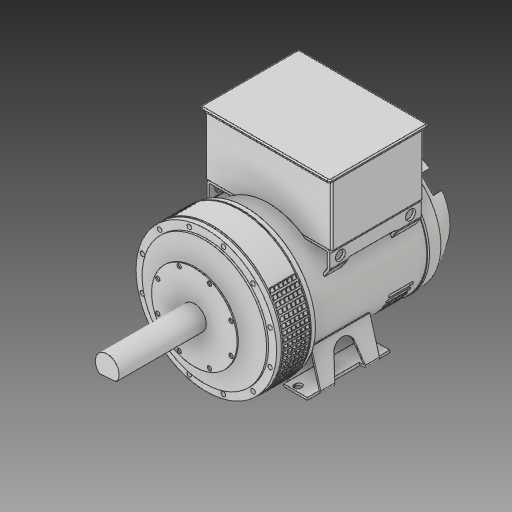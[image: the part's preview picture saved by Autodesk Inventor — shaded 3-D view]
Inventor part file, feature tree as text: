
AUTODESK INVENTOR PART (.ipt)
format: ipt  version: 2018 (Build 220112000, 112)  size: 3,364,864 bytes
history: native  units: in
note: dims shown in document units (in); Inventor stores cm internally (conversion verified against a paired STEP export)
features: other x14, extrude x1, sketch x1
ambient origin geometry x8: Origin, YZ Plane, XZ Plane, XY Plane, X Axis, Y Axis, Z Axis, Center Point
bodies: Solid1 (feature_tree), Solid2 (feature_tree), Solid3 (feature_tree), Solid4 (feature_tree), Solid5 (feature_tree), Solid6 (feature_tree), Solid7 (feature_tree), Solid8 (feature_tree), Solid9 (feature_tree), Solid10 (feature_tree), Solid11 (feature_tree), Solid12 (feature_tree)
feature tree (16):
  other  "Part5.ipt"
  extrude  "Extrusion1"  Depth=101.6875in TaperAngle=0.0deg
  other  "Solid1::Part5.ipt"
  other  "Solid2::Part5.ipt"
  other  "Solid3::Part5.ipt"
  other  "Solid4::Part5.ipt"
  other  "Solid5::Part5.ipt"
  other  "Solid6::Part5.ipt"
  other  "Solid7::Part5.ipt"
  other  "Solid8::Part5.ipt"
  other  "Solid9::Part5.ipt"
  other  "Solid10::Part5.ipt"
  other  "Solid11::Part5.ipt"
  other  "Solid12::Part5.ipt"
  other  "TaggingFeature1"
  sketch  "Sketch1"  dims[d0=4.7244in d1=101.6875in d2=0.0in]
